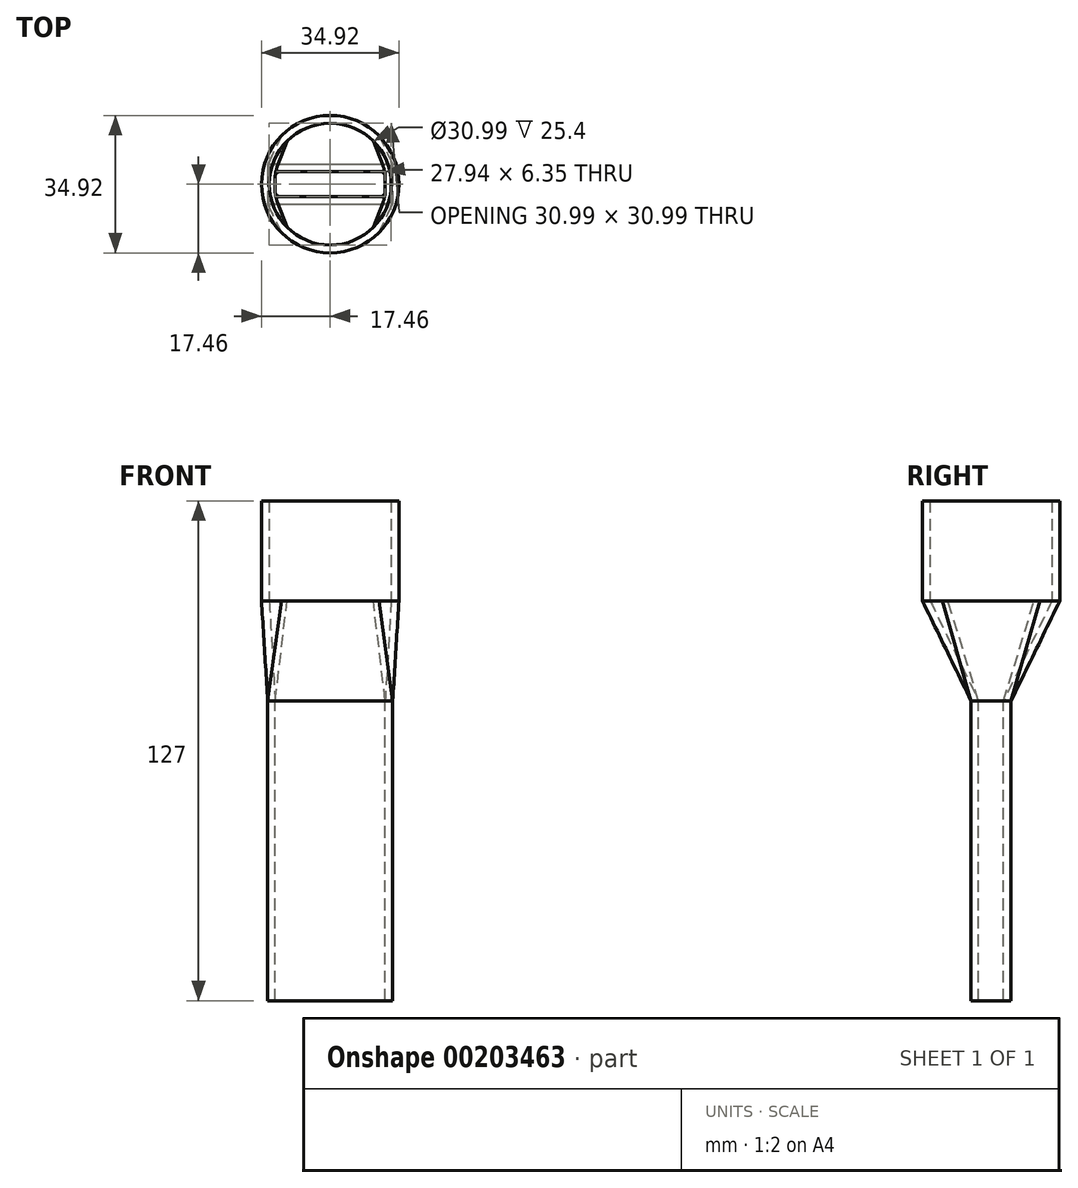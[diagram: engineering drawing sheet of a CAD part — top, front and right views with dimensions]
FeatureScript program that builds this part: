
annotation { "Feature Type Name" : "Feature", "Feature Type Description" : "" }
export const myFeature = defineFeature(function(context is Context, id is Id, definition is map)
    precondition{}
    {
        {
            var Q0;
            Q0=qCreatedBy(makeId("Top.planeOp"),FACE);
            var sketch = newSketch(context, id + "F0", { "sketchPlane" : qUnion([Q0])});
            skLineSegment(sketch, "E0.bottom", {"start": v(-15.88, 5.08) * mm, "end": v(15.88, 5.08) * mm});
            skLineSegment(sketch, "E0.top", {"start": v(-15.88, -5.08) * mm, "end": v(15.88, -5.08) * mm});
            skLineSegment(sketch, "E0.left", {"start": v(-15.88, 5.08) * mm, "end": v(-15.88, -5.08) * mm});
            skLineSegment(sketch, "E0.right", {"start": v(15.88, 5.08) * mm, "end": v(15.88, -5.08) * mm});
            skLineSegment(sketch, "E1", {"start": v(0, 0) * mm, "end": v(0, 5.08) * mm, "construction": true});
            skLineSegment(sketch, "E2", {"start": v(0, 0) * mm, "end": v(15.88, 0) * mm, "construction": true});
            skPoint(sketch, "E3.visualSharp", {"position": v(-15.88, 5.08) * mm});
            skPoint(sketch, "E4.visualSharp", {"position": v(-15.88, -5.08) * mm});
            skPoint(sketch, "E5.visualSharp", {"position": v(15.88, -5.08) * mm});
            skPoint(sketch, "E6.visualSharp", {"position": v(15.88, 5.08) * mm});
            skSolve(sketch);
        }
        {
            var Q0;
            Q0=makeQuery(id+"F0.imprint","IMPRINT",FACE,{"disambiguationData":[TD([[makeQuery(id+"F0.imprint","IMPRINT",EDGE,{"derivedFrom":sQuery(id+"F0.wireOp",EDGE,"E0.bottom")}),-1.0]])]});
            extrude(context, id + "F1", {"entities" : qUnion([Q0]), "depth" : 76.2 * mm});
        }
        {
            var Q0;
            Q0=makeQuery(id+"F1.opExtrude","CAP_FACE",FACE,{"disambiguationData":[OSD([sQuery(id+"F0.wireOp",EDGE,"E0.bottom"),sQuery(id+"F0.wireOp",EDGE,"E0.top"),sQuery(id+"F0.wireOp",EDGE,"E0.left"),sQuery(id+"F0.wireOp",EDGE,"E0.right"),sQuery(id+"F0.wireOp",EDGE,"E3.filletArc"),sQuery(id+"F0.wireOp",EDGE,"E4.filletArc"),sQuery(id+"F0.wireOp",EDGE,"E5.filletArc"),sQuery(id+"F0.wireOp",EDGE,"E6.filletArc"),sQuery(id+"F0.wireOp",EDGE,"e7cc14a2-017c-43af-a9cb-176855c41ff1.0"),sQuery(id+"F0.wireOp",EDGE,"e7cc14a2-017c-43af-a9cb-176855c41ff1.1"),sQuery(id+"F0.wireOp",EDGE,"e7cc14a2-017c-43af-a9cb-176855c41ff1.2"),sQuery(id+"F0.wireOp",EDGE,"e7cc14a2-017c-43af-a9cb-176855c41ff1.3"),sQuery(id+"F0.wireOp",EDGE,"7a796098-04e0-4154-ae6f-b04121a63667.filletArc"),sQuery(id+"F0.wireOp",EDGE,"bbcdf0b4-7c3c-4edd-a4b0-931265a29f67.filletArc"),sQuery(id+"F0.wireOp",EDGE,"7c8593b5-b22a-493e-b1b3-677a3aafa16c.filletArc"),sQuery(id+"F0.wireOp",EDGE,"e2697efe-fd5a-4384-9e21-30a783082e75.filletArc")])],"isStart":false});
            cPlane(context, id + "F2", {"entities" : qUnion([Q0]), "cplaneType" : CPlaneType.OFFSET, "offset" : 25.4 * mm, "width" : 152.4 * mm, "height" : 152.4 * mm});
        }
        {
            var Q0;
            Q0=qCreatedBy(id+"F2.planeOp",FACE);
            var sketch = newSketch(context, id + "F3", { "sketchPlane" : qUnion([Q0])});
            skCircle(sketch, "E7", {"center": v(0, 0) * mm, "radius": 17.46 * mm});
            skSolve(sketch);
        }
        {
            var Q0;
            Q0=makeQuery(id+"F3.imprint","IMPRINT",FACE,{"disambiguationData":[TD([[makeQuery(id+"F3.imprint","IMPRINT",EDGE,{"derivedFrom":sQuery(id+"F3.wireOp",EDGE,"d9iNpvHc-Ba0O-HXKU-9EuX-Hbc5Z30B9kPa")}),-1.0]])]});
            var Q1;
            Q1=makeQuery(id+"F3.imprint","IMPRINT",FACE,{"disambiguationData":[TD([[makeQuery(id+"F3.imprint","IMPRINT",EDGE,{"derivedFrom":sQuery(id+"F3.wireOp",EDGE,"E7")}),1.0]])]});
            extrude(context, id + "F4", {"entities" : qUnion([Q0, Q1]), "operationType" : NewBodyOperationType.ADD, "depth" : 25.4 * mm});
        }
        {
            var Q0;
            Q0=makeQuery(id+"F4.opExtrude","CAP_FACE",FACE,{"disambiguationData":[OSD([sQuery(id+"F3.wireOp",EDGE,"E7")])],"isStart":true});
            var sketch = newSketch(context, id + "F5", { "sketchPlane" : qUnion([Q0])});
            skLineSegment(sketch, "E8", {"start": v(0, 0) * mm, "end": v(-10.26, 0) * mm, "construction": true});
            skLineSegment(sketch, "E9", {"start": v(0, 0) * mm, "end": v(0, 7.36) * mm, "construction": true});
            skLineSegment(sketch, "E10", {"start": v(-12.35, 12.35) * mm, "end": v(12.35, -12.35) * mm, "construction": true});
            skLineSegment(sketch, "E11", {"start": v(-12.35, -12.35) * mm, "end": v(12.35, 12.35) * mm, "construction": true});
            skSolve(sketch);
        }
        {
            var Q0;
            Q0=makeQuery(id+"F4.opExtrude","CAP_FACE",FACE,{"disambiguationData":[OSD([sQuery(id+"F3.wireOp",EDGE,"E7")])],"isStart":true});
            var Q1;
            Q1=makeQuery(id+"F1.opExtrude","CAP_FACE",FACE,{"disambiguationData":[OSD([sQuery(id+"F0.wireOp",EDGE,"E0.bottom"),sQuery(id+"F0.wireOp",EDGE,"E0.top"),sQuery(id+"F0.wireOp",EDGE,"E0.left"),sQuery(id+"F0.wireOp",EDGE,"E0.right")])],"isStart":false});
            var Q2;
            Q2=sQuery(id+"F5.wireOp",VERTEX,"E10.start");
            var Q3;
            Q3=makeQuery(id+"F1.opExtrude","CAP_VERTEX",VERTEX,{"disambiguationData":[OSD([sQuery(id+"F0.wireOp",EDGE,"E0.top"),sQuery(id+"F0.wireOp",EDGE,"E0.left")])],"isStart":false});
            loft(context, id + "F6", {"sheetProfilesArray" : [{ "sheetProfileEntities" : qUnion([Q0]) }, { "sheetProfileEntities" : qUnion([Q1]) }], "matchConnections" : true, "connections" : [{ "connectionEntities" : qUnion([Q2, Q3]), "connectionEdgeQueries" : qUnion([]), "connectionEdgeParameters" : [] }]});
        }
        {
            var Q0;
            Q0=makeQuery(id+"F4.opExtrude","CAP_FACE",FACE,{"disambiguationData":[OSD([sQuery(id+"F3.wireOp",EDGE,"E7")])],"isStart":true});
            var sketch = newSketch(context, id + "F7", { "sketchPlane" : qUnion([Q0])});
            skCircle(sketch, "E12", {"center": v(0, 0) * mm, "radius": 15.5 * mm});
            skLineSegment(sketch, "E13", {"start": v(0, 0) * mm, "end": v(-8.37, 0) * mm, "construction": true});
            skLineSegment(sketch, "E14", {"start": v(-10.96, -10.96) * mm, "end": v(10.96, 10.96) * mm, "construction": true});
            skLineSegment(sketch, "E15", {"start": v(-10.96, 10.96) * mm, "end": v(10.96, -10.96) * mm, "construction": true});
            skSolve(sketch);
        }
        {
            var Q0;
            Q0=makeQuery(id+"F1.opExtrude","CAP_FACE",FACE,{"disambiguationData":[OSD([sQuery(id+"F0.wireOp",EDGE,"E0.bottom"),sQuery(id+"F0.wireOp",EDGE,"E0.top"),sQuery(id+"F0.wireOp",EDGE,"E0.left"),sQuery(id+"F0.wireOp",EDGE,"E0.right")])],"isStart":false});
            var sketch = newSketch(context, id + "F8", { "sketchPlane" : qUnion([Q0])});
            skLineSegment(sketch, "E16.0", {"start": v(-13.97, 3.18) * mm, "end": v(13.97, 3.18) * mm});
            skLineSegment(sketch, "E16.1", {"start": v(-13.97, 3.18) * mm, "end": v(-13.97, -3.18) * mm});
            skLineSegment(sketch, "E16.2", {"start": v(-13.97, -3.18) * mm, "end": v(13.97, -3.18) * mm});
            skLineSegment(sketch, "E16.3", {"start": v(13.97, 3.18) * mm, "end": v(13.97, -3.18) * mm});
            skSolve(sketch);
        }
        {
            var Q1;
            Q1=makeQuery(id+"F8.imprint","IMPRINT",FACE,{"disambiguationData":[TD([[makeQuery(id+"F8.imprint","IMPRINT",EDGE,{"derivedFrom":sQuery(id+"F8.wireOp",EDGE,"E16.0")}),-1.0]])]});
            var Q2;
            Q2=makeQuery(id+"F7.imprint","IMPRINT",FACE,{"disambiguationData":[TD([[makeQuery(id+"F7.imprint","IMPRINT",EDGE,{"derivedFrom":sQuery(id+"F7.wireOp",EDGE,"E12")}),1.0]])]});
            var Q3;
            Q3=sQuery(id+"F7.wireOp",VERTEX,"E14.start");
            var Q4;
            Q4=sQuery(id+"F8.wireOp",VERTEX,"E16.1.start");
            loft(context, id + "F9", {"operationType" : NewBodyOperationType.REMOVE, "sheetProfilesArray" : [{ "sheetProfileEntities" : qUnion([Q1]) }, { "sheetProfileEntities" : qUnion([Q2]) }], "matchConnections" : true, "connections" : [{ "connectionEntities" : qUnion([Q3, Q4]), "connectionEdgeQueries" : qUnion([]), "connectionEdgeParameters" : [] }]});
        }
        {
            var Q0;
            Q0 = qSketchRegion(id + "F8", true);
            extrude(context, id + "F10", {"entities" : qUnion([Q0]), "operationType" : NewBodyOperationType.REMOVE, "endBound" : BoundingType.UP_TO_NEXT, "oppositeDirection" : true, "depth" : 25.4 * mm});
        }
        {
            var Q0;
            Q0 = qSketchRegion(id + "F7", true);
            extrude(context, id + "F11", {"entities" : qUnion([Q0]), "operationType" : NewBodyOperationType.REMOVE, "endBound" : BoundingType.UP_TO_NEXT, "oppositeDirection" : true, "depth" : 25.4 * mm});
        }
        {
            var Q0;
            Q0=makeQuery(id+"F10.boolean.opBoolean","COPY",EDGE,{"derivedFrom":makeQuery(id+"F10.opExtrude","SWEPT_EDGE",EDGE,{"disambiguationData":[OSD([sQuery(id+"F8.wireOp",EDGE,"E16.0"),sQuery(id+"F8.wireOp",EDGE,"E16.3")])]})});
            var Q1;
            Q1=makeQuery(id+"F10.boolean.opBoolean","COPY",EDGE,{"derivedFrom":makeQuery(id+"F10.opExtrude","SWEPT_EDGE",EDGE,{"disambiguationData":[OSD([sQuery(id+"F8.wireOp",EDGE,"E16.2"),sQuery(id+"F8.wireOp",EDGE,"E16.3")])]})});
            var Q2;
            Q2=makeQuery(id+"F10.boolean.opBoolean","COPY",EDGE,{"derivedFrom":makeQuery(id+"F10.opExtrude","SWEPT_EDGE",EDGE,{"disambiguationData":[OSD([sQuery(id+"F8.wireOp",EDGE,"E16.1"),sQuery(id+"F8.wireOp",EDGE,"E16.2")])]})});
            var Q3;
            Q3=makeQuery(id+"F10.boolean.opBoolean","COPY",EDGE,{"derivedFrom":makeQuery(id+"F10.opExtrude","SWEPT_EDGE",EDGE,{"disambiguationData":[OSD([sQuery(id+"F8.wireOp",EDGE,"E16.0"),sQuery(id+"F8.wireOp",EDGE,"E16.1")])]})});
            fillet(context, id + "F12", {"entities" : qUnion([Q0, Q1, Q2, Q3]), "radius" : 1.27 * mm, "tangentPropagation" : true, "allowEdgeOverflow" : false});
        }
        {
            var Q0;
            Q0=makeQuery(id+"F1.opExtrude","SWEPT_EDGE",EDGE,{"disambiguationData":[OSD([sQuery(id+"F0.wireOp",EDGE,"E0.top"),sQuery(id+"F0.wireOp",EDGE,"E0.left")])]});
            var Q1;
            Q1=makeQuery(id+"F1.opExtrude","SWEPT_EDGE",EDGE,{"disambiguationData":[OSD([sQuery(id+"F0.wireOp",EDGE,"E0.top"),sQuery(id+"F0.wireOp",EDGE,"E0.right")])]});
            var Q2;
            Q2=makeQuery(id+"F1.opExtrude","SWEPT_EDGE",EDGE,{"disambiguationData":[OSD([sQuery(id+"F0.wireOp",EDGE,"E0.bottom"),sQuery(id+"F0.wireOp",EDGE,"E0.right")])]});
            var Q3;
            Q3=makeQuery(id+"F1.opExtrude","SWEPT_EDGE",EDGE,{"disambiguationData":[OSD([sQuery(id+"F0.wireOp",EDGE,"E0.bottom"),sQuery(id+"F0.wireOp",EDGE,"E0.left")])]});
            fillet(context, id + "F13", {"entities" : qUnion([Q0, Q1, Q2, Q3]), "radius" : 2.54 * mm, "tangentPropagation" : true, "allowEdgeOverflow" : false});
        }
    });
